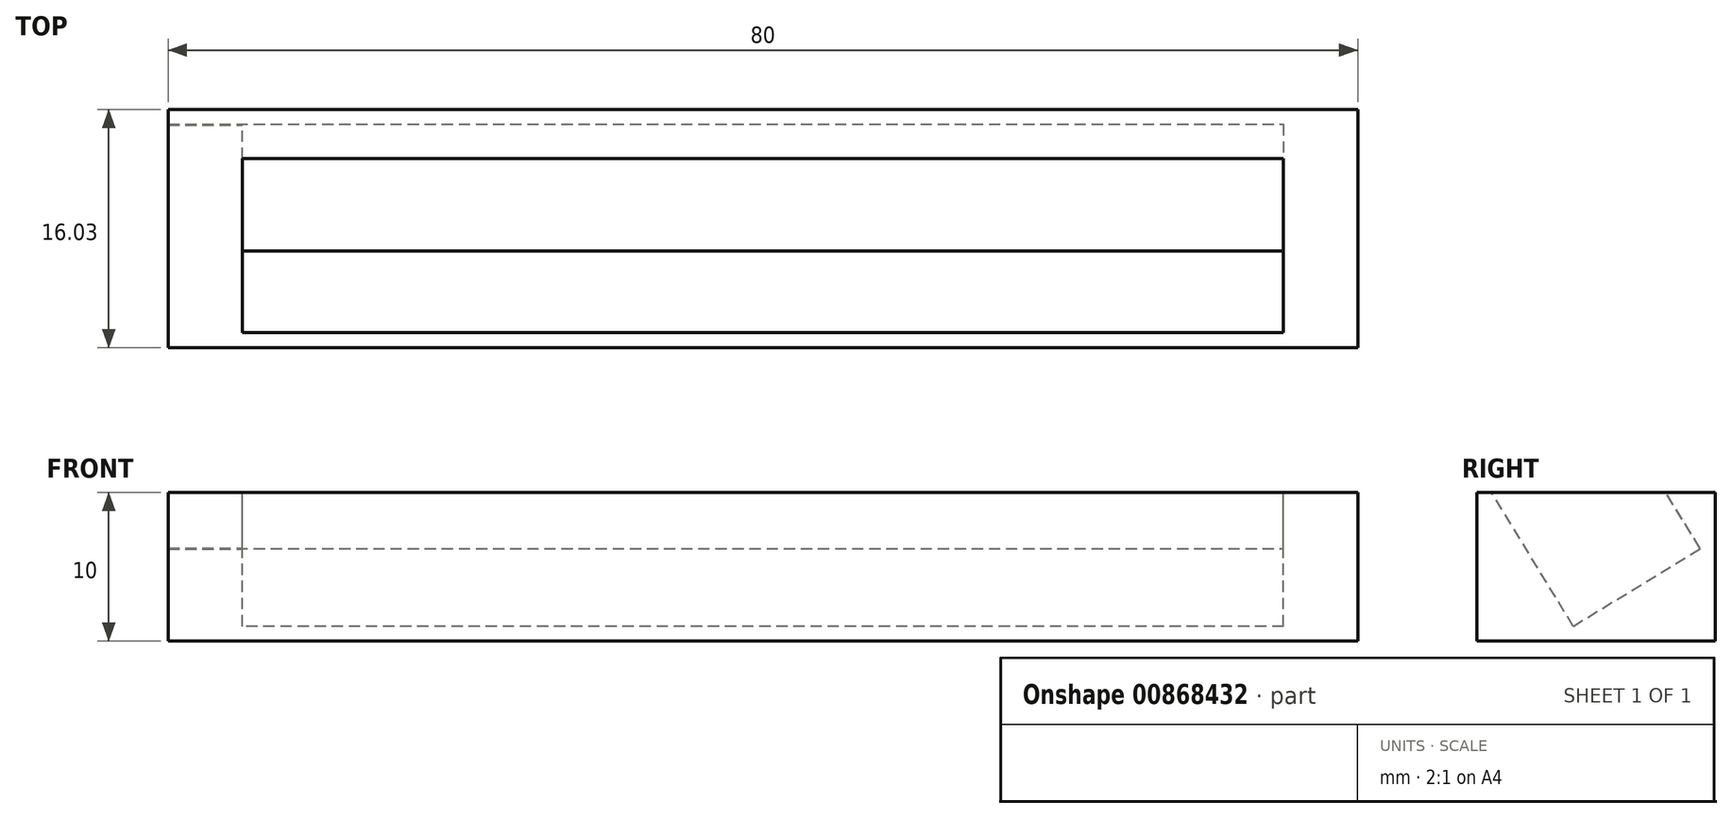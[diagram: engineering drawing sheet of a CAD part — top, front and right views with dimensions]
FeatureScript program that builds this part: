
annotation { "Feature Type Name" : "Feature", "Feature Type Description" : "" }
export const myFeature = defineFeature(function(context is Context, id is Id, definition is map)
    precondition{}
    {
        {
            var Q0;
            Q0=qCreatedBy(makeId("Right.planeOp"),FACE);
            var sketch = newSketch(context, id + "F0", { "sketchPlane" : qUnion([Q0])});
            skLineSegment(sketch, "E0", {"start": v(0, 0) * mm, "end": v(7.5, 0) * mm});
            skLineSegment(sketch, "E1", {"start": v(7.5, 0) * mm, "end": v(7.5, 10) * mm});
            skLineSegment(sketch, "E2", {"start": v(7.5, 10) * mm, "end": v(-7.5, 10) * mm});
            skLineSegment(sketch, "E3", {"start": v(-7.5, 10) * mm, "end": v(-7.5, 0) * mm});
            skLineSegment(sketch, "E4", {"start": v(-7.5, 0) * mm, "end": v(0, 0) * mm});
            skSolve(sketch);
        }
        {
            var Q0;
            Q0=makeQuery(id+"F0.imprint","IMPRINT",FACE,{"disambiguationData":[TD([[makeQuery(id+"F0.imprint","IMPRINT",EDGE,{"derivedFrom":sQuery(id+"F0.wireOp",EDGE,"E0")}),1.0]])]});
            extrude(context, id + "F1", {"entities" : qUnion([Q0]), "depth" : 5 * mm, "offsetDistance" : 25 * mm});
        }
        {
            var Q0;
            Q0=makeQuery(id+"F1.opExtrude","CAP_FACE",FACE,{"disambiguationData":[OSD([sQuery(id+"F0.wireOp",EDGE,"E0"),sQuery(id+"F0.wireOp",EDGE,"E1"),sQuery(id+"F0.wireOp",EDGE,"E2"),sQuery(id+"F0.wireOp",EDGE,"E3"),sQuery(id+"F0.wireOp",EDGE,"E4")])],"isStart":false});
            var sketch = newSketch(context, id + "F2", { "sketchPlane" : qUnion([Q0])});
            skLineSegment(sketch, "E5", {"start": v(0, 0) * mm, "end": v(0, 1) * mm});
            skLineSegment(sketch, "E6", {"start": v(0, 1) * mm, "end": v(6.5, 1) * mm});
            skLineSegment(sketch, "E7", {"start": v(6.5, 1) * mm, "end": v(6.5, 5.58) * mm});
            skLineSegment(sketch, "E8", {"start": v(-5.89, 9) * mm, "end": v(-6.5, 9) * mm});
            skLineSegment(sketch, "E9", {"start": v(-6.5, 9) * mm, "end": v(-6.5, 1) * mm});
            skLineSegment(sketch, "E10", {"start": v(-6.5, 1) * mm, "end": v(0, 1) * mm});
            skLineSegment(sketch, "E11", {"start": v(0, 1) * mm, "end": v(-1, 1) * mm});
            skLineSegment(sketch, "E12", {"start": v(-1, 1) * mm, "end": v(-6.5, 10) * mm});
            skLineSegment(sketch, "E13", {"start": v(-1, 1) * mm, "end": v(7.53, 6.21) * mm});
            skLineSegment(sketch, "E14", {"start": v(7.53, 6.21) * mm, "end": v(5.22, 10) * mm});
            skLineSegment(sketch, "E15", {"start": v(7.53, 6.21) * mm, "end": v(8.53, 6.21) * mm});
            skLineSegment(sketch, "E16", {"start": v(7.5, 10) * mm, "end": v(8.53, 10) * mm});
            skLineSegment(sketch, "E17", {"start": v(8.53, 10) * mm, "end": v(8.53, 0) * mm});
            skLineSegment(sketch, "E18", {"start": v(8.53, 0) * mm, "end": v(7.5, 0) * mm});
            skSolve(sketch);
        }
        {
            var Q0;
            {var subQ1=sQuery(id+"F2.wireOp",EDGE,"E15");Q0=makeQuery(id+"F2.imprint","IMPRINT",FACE,{"disambiguationData":[TD([[makeQuery(id+"F2.imprint","IMPRINT",EDGE,{"derivedFrom":subQ1}),1.0]])]});}
            var Q1;
            {var subQ2=sQuery(id+"F2.wireOp",EDGE,"E15");Q1=makeQuery(id+"F2.imprint","IMPRINT",FACE,{"disambiguationData":[TD([[makeQuery(id+"F2.imprint","IMPRINT",EDGE,{"derivedFrom":subQ2}),-1.0]])]});}
            extrude(context, id + "F3", {"entities" : qUnion([Q0, Q1]), "operationType" : NewBodyOperationType.ADD, "oppositeDirection" : true, "depth" : 5 * mm, "offsetDistance" : 25 * mm});
        }
        {
            var Q0;
            {var subQ5=sQuery(id+"F2.wireOp",EDGE,"E5");Q0=makeQuery(id+"F2.imprint","IMPRINT",FACE,{"disambiguationData":[TD([[makeQuery(id+"F2.imprint","IMPRINT",EDGE,{"derivedFrom":subQ5}),1.0]])]});}
            var Q1;
            {var subQ0=sQuery(id+"F2.wireOp",EDGE,"E8");Q1=makeQuery(id+"F2.imprint","IMPRINT",FACE,{"disambiguationData":[TD([[makeQuery(id+"F2.imprint","IMPRINT",EDGE,{"derivedFrom":subQ0}),1.0]])]});}
            var Q2;
            Q2=makeQuery(id+"F2.imprint","IMPRINT",FACE,{"disambiguationData":[TD([[makeQuery(id+"F2.imprint","IMPRINT",EDGE,{"derivedFrom":sQuery(id+"F2.wireOp",EDGE,"E6")}),1.0]])]});
            var Q3;
            {var subQ2=sQuery(id+"F2.wireOp",EDGE,"E15");Q3=makeQuery(id+"F2.imprint","IMPRINT",FACE,{"disambiguationData":[TD([[makeQuery(id+"F2.imprint","IMPRINT",EDGE,{"derivedFrom":subQ2}),-1.0]])]});}
            var Q4;
            {var subQ4=sQuery(id+"F2.wireOp",EDGE,"E5");Q4=makeQuery(id+"F2.imprint","IMPRINT",FACE,{"disambiguationData":[TD([[makeQuery(id+"F2.imprint","IMPRINT",EDGE,{"derivedFrom":subQ4}),-1.0]])]});}
            var Q5;
            {var subQ1=sQuery(id+"F2.wireOp",EDGE,"E15");Q5=makeQuery(id+"F2.imprint","IMPRINT",FACE,{"disambiguationData":[TD([[makeQuery(id+"F2.imprint","IMPRINT",EDGE,{"derivedFrom":subQ1}),1.0]])]});}
            var Q6;
            {var subQ0=sQuery(id+"F2.wireOp",EDGE,"E14");var subQ1=makeQuery(id+"F1.opExtrude","CAP_EDGE",EDGE,{"disambiguationData":[OSD([sQuery(id+"F0.wireOp",EDGE,"E2")])],"isStart":false});var subQ2=makeQuery(id+"F2.imprint","INTERSECT",VERTEX,{"derivedFrom":[subQ1,subQ0]});Q6=makeQuery(id+"F2.imprint","IMPRINT",FACE,{"disambiguationData":[TD([[makeQuery(id+"F2.imprint","IMPRINT",EDGE,{"disambiguationData":[TD([[subQ2,1.0]])],"derivedFrom":subQ0}),-1.0]])]});}
            extrude(context, id + "F4", {"entities" : qUnion([Q0, Q1, Q2, Q3, Q4, Q5, Q6]), "operationType" : NewBodyOperationType.ADD, "depth" : 70 * mm, "offsetDistance" : 25 * mm});
        }
        {
            var Q0;
            Q0=makeQuery(id+"F4.opExtrude","CAP_FACE",FACE,{"disambiguationData":[OSD([sQuery(id+"F0.wireOp",EDGE,"E0"),sQuery(id+"F0.wireOp",EDGE,"E2"),sQuery(id+"F0.wireOp",EDGE,"E3"),sQuery(id+"F0.wireOp",EDGE,"E4"),sQuery(id+"F2.wireOp",EDGE,"E12"),sQuery(id+"F2.wireOp",EDGE,"E13"),sQuery(id+"F2.wireOp",EDGE,"E14"),sQuery(id+"F2.wireOp",EDGE,"E16"),sQuery(id+"F2.wireOp",EDGE,"E17"),sQuery(id+"F2.wireOp",EDGE,"E18")])],"isStart":false});
            var sketch = newSketch(context, id + "F5", { "sketchPlane" : qUnion([Q0])});
            skLineSegment(sketch, "E19.bottom", {"start": v(-7.5, 0) * mm, "end": v(8.53, 0) * mm});
            skLineSegment(sketch, "E19.top", {"start": v(-7.5, 10) * mm, "end": v(8.53, 10) * mm});
            skLineSegment(sketch, "E19.left", {"start": v(-7.5, 0) * mm, "end": v(-7.5, 10) * mm});
            skLineSegment(sketch, "E19.right", {"start": v(8.53, 0) * mm, "end": v(8.53, 10) * mm});
            skSolve(sketch);
        }
        {
            var Q0;
            Q0=makeQuery(id+"F5.imprint","IMPRINT",FACE,{"disambiguationData":[TD([[makeQuery(id+"F5.imprint","IMPRINT",EDGE,{"derivedFrom":sQuery(id+"F5.wireOp",EDGE,"E19.bottom")}),1.0]])]});
            var Q1;
            {var subQ1=makeQuery(id+"F4.opExtrude","CAP_EDGE",EDGE,{"disambiguationData":[OSD([sQuery(id+"F2.wireOp",EDGE,"E12")])],"isStart":false});Q1=makeQuery(id+"F5.imprint","IMPRINT",FACE,{"disambiguationData":[TD([[makeQuery(id+"F5.imprint","IMPRINT",EDGE,{"derivedFrom":subQ1}),-1.0]])]});}
            extrude(context, id + "F6", {"entities" : qUnion([Q0, Q1]), "operationType" : NewBodyOperationType.ADD, "depth" : 5 * mm, "offsetDistance" : 25 * mm});
        }
        {
            var Q0;
            Q0=makeQuery(id+"F1.opExtrude","SWEPT_BODY",BODY,{"disambiguationData":[OSD([sQuery(id+"F0.wireOp",EDGE,"E0"),sQuery(id+"F0.wireOp",EDGE,"E1"),sQuery(id+"F0.wireOp",EDGE,"E2"),sQuery(id+"F0.wireOp",EDGE,"E3"),sQuery(id+"F0.wireOp",EDGE,"E4")])]});
            transform(context, id + "F7", {"entities" : qUnion([Q0]), "transformType" : TransformType.TRANSLATION_3D, "dx" : -40 * mm, "dy" : 0 * mm, "dz" : 0 * mm, "makeCopy" : false});
        }
    });
